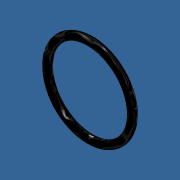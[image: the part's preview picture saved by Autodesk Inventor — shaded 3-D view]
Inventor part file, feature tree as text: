
AUTODESK INVENTOR PART (.ipt)
format: ipt  version: 2018 (Build 220112000, 112)  size: 139,264 bytes
history: native  units: mm
features: revolve x1, sketch x1
ambient origin geometry x8: Origin, YZ Plane, XZ Plane, XY Plane, X Axis, Y Axis, Z Axis, Center Point
bodies: Solid1 (feature_tree)
feature tree (2):
  revolve  "Revolution1"  [1 undecoded]
  sketch  "Sketch2"  dims[d0=33.0mm d1=16.5mm d2=0.0mm d3=3.0mm d4=90.0deg]
note: 1 required parameter value undecoded (feature->parameter linkage not recoverable at this tier; creation-order binding heuristic only, values carry confidence <= 0.55)
